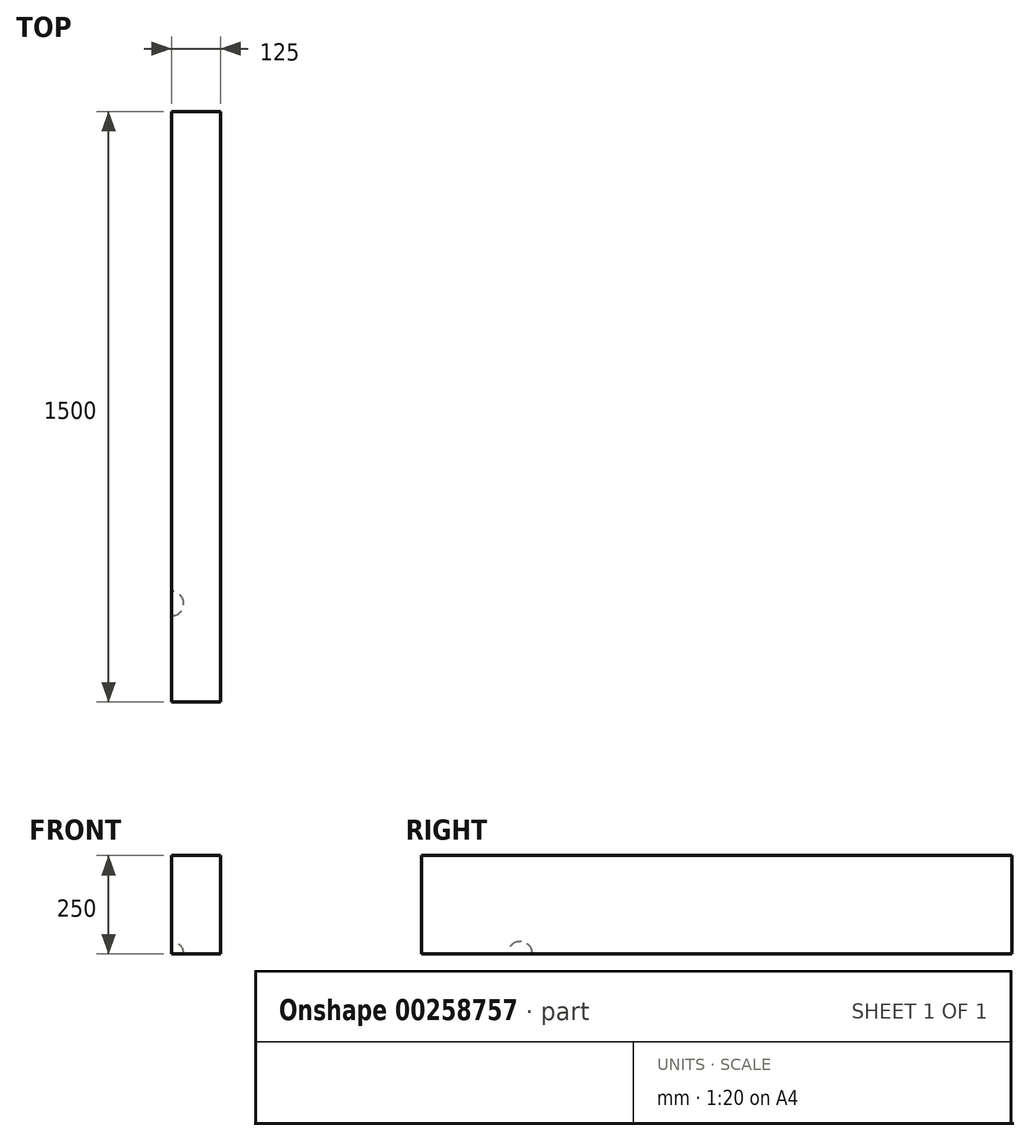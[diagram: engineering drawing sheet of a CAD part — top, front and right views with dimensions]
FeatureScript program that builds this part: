
annotation { "Feature Type Name" : "Feature", "Feature Type Description" : "" }
export const myFeature = defineFeature(function(context is Context, id is Id, definition is map)
    precondition{}
    {
        {
            var Q0;
            Q0=qCreatedBy(makeId("Front.planeOp"),FACE);
            var sketch = newSketch(context, id + "F0", { "sketchPlane" : qUnion([Q0])});
            skLineSegment(sketch, "E0.bottom", {"start": v(0, 0) * mm, "end": v(125, 0) * mm});
            skLineSegment(sketch, "E0.top", {"start": v(0, 250) * mm, "end": v(125, 250) * mm});
            skLineSegment(sketch, "E0.left", {"start": v(0, 0) * mm, "end": v(0, 250) * mm});
            skLineSegment(sketch, "E0.right", {"start": v(125, 0) * mm, "end": v(125, 250) * mm});
            skSolve(sketch);
        }
        {
            var Q0;
            Q0=makeQuery(id+"F0.imprint","IMPRINT",FACE,{"disambiguationData":[TD([[makeQuery(id+"F0.imprint","IMPRINT",EDGE,{"derivedFrom":sQuery(id+"F0.wireOp",EDGE,"E0.bottom")}),1.0]])]});
            extrude(context, id + "F1", {"entities" : qUnion([Q0]), "depth" : 250 * mm});
        }
        {
            var Q0;
            Q0=makeQuery(id+"F1.opExtrude","CAP_FACE",FACE,{"disambiguationData":[OSD([sQuery(id+"F0.wireOp",EDGE,"E0.bottom"),sQuery(id+"F0.wireOp",EDGE,"E0.top"),sQuery(id+"F0.wireOp",EDGE,"E0.left"),sQuery(id+"F0.wireOp",EDGE,"E0.right")])],"isStart":true});
            extrude(context, id + "F2", {"entities" : qUnion([Q0]), "operationType" : NewBodyOperationType.ADD, "depth" : 1250 * mm});
        }
        {
            var Q0;
            Q0=qCreatedBy(makeId("Front.planeOp"),FACE);
            var sketch = newSketch(context, id + "F3", { "sketchPlane" : qUnion([Q0])});
            skArc(sketch, "E1", {"start": v(0, 31.4) * mm, "mid": v(22.2, 22.2) * mm, "end": v(31.4, 0) * mm});
            skLineSegment(sketch, "E2", {"start": v(0, 31.4) * mm, "end": v(0, 0) * mm});
            skLineSegment(sketch, "E3", {"start": v(31.4, 0) * mm, "end": v(0, 0) * mm});
            skSolve(sketch);
        }
        {
            var Q0;
            Q0 = qSketchRegion(id + "F3", true);
            var Q1;
            Q1=sQuery(id+"F3.wireOp",EDGE,"E2");
            revolve(context, id + "F4", {"operationType" : NewBodyOperationType.REMOVE, "entities" : qUnion([Q0]), "axis" : qUnion([Q1]), "revolveType" : RevolveType.FULL, "oppositeDirection" : true});
        }
    });
